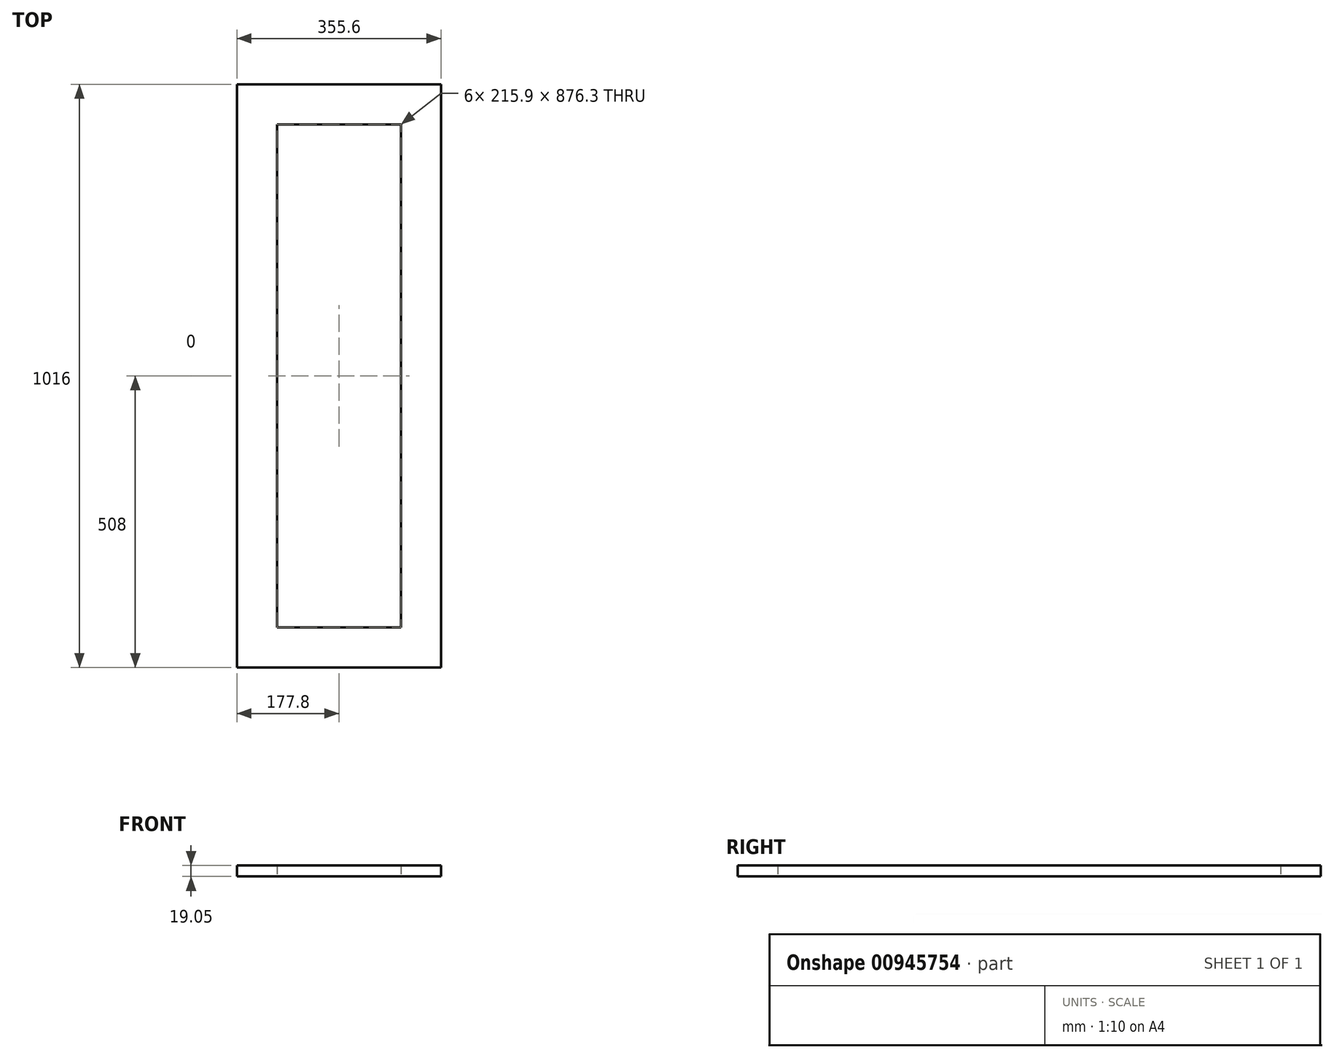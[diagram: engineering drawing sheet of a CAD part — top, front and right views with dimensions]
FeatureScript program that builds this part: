
annotation { "Feature Type Name" : "Feature", "Feature Type Description" : "" }
export const myFeature = defineFeature(function(context is Context, id is Id, definition is map)
    precondition{}
    {
        {
            var Q0;
            Q0=qCreatedBy(makeId("Top.planeOp"),FACE);
            var sketch = newSketch(context, id + "F0", { "sketchPlane" : qUnion([Q0])});
            skLineSegment(sketch, "E0.bottom", {"start": v(177.8, 508) * mm, "end": v(-177.8, 508) * mm});
            skLineSegment(sketch, "E0.top", {"start": v(177.8, -508) * mm, "end": v(-177.8, -508) * mm});
            skLineSegment(sketch, "E0.left", {"start": v(177.8, 508) * mm, "end": v(177.8, -508) * mm});
            skLineSegment(sketch, "E0.right", {"start": v(-177.8, 508) * mm, "end": v(-177.8, -508) * mm});
            skPoint(sketch, "E0.middle", {"position": v(0, 0) * mm});
            skLineSegment(sketch, "E1.bottom", {"start": v(107.95, 438.15) * mm, "end": v(-107.95, 438.15) * mm});
            skLineSegment(sketch, "E1.top", {"start": v(107.95, -438.15) * mm, "end": v(-107.95, -438.15) * mm});
            skLineSegment(sketch, "E1.left", {"start": v(107.95, 438.15) * mm, "end": v(107.95, -438.15) * mm});
            skLineSegment(sketch, "E1.right", {"start": v(-107.95, 438.15) * mm, "end": v(-107.95, -438.15) * mm});
            skSolve(sketch);
        }
        {
            var Q0;
            Q0=makeQuery(id+"F0.imprint","IMPRINT",FACE,{"disambiguationData":[TD([[makeQuery(id+"F0.imprint","IMPRINT",EDGE,{"derivedFrom":sQuery(id+"F0.wireOp",EDGE,"E0.bottom")}),1.0]])]});
            extrude(context, id + "F1", {"entities" : qUnion([Q0]), "depth" : 19.05 * mm, "offsetDistance" : 25.4 * mm});
        }
    });
